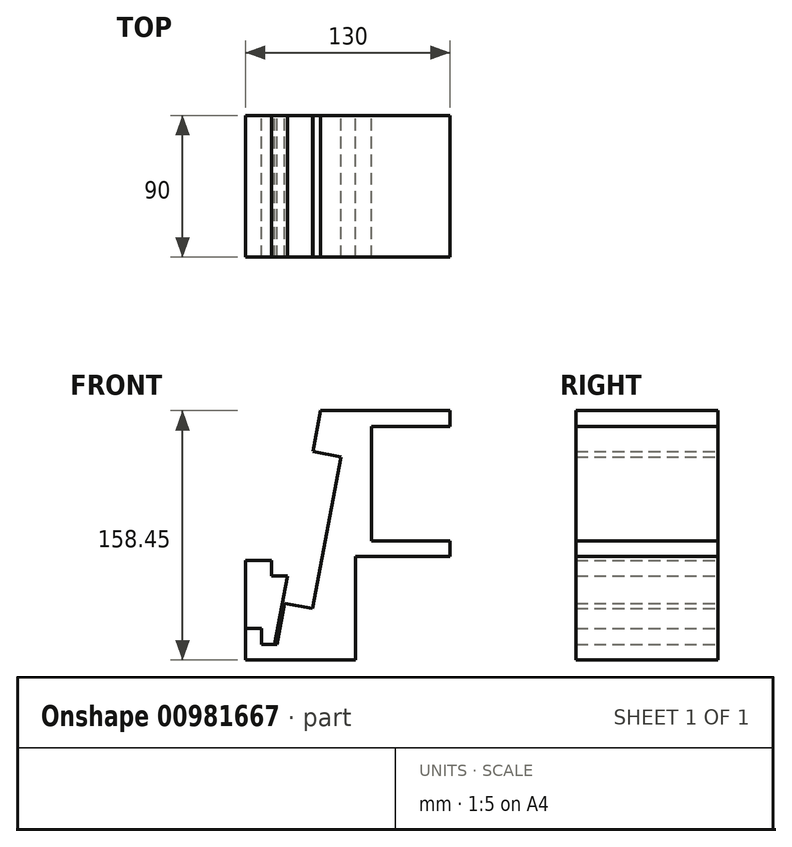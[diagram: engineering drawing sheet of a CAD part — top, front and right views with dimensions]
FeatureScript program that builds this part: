
annotation { "Feature Type Name" : "Feature", "Feature Type Description" : "" }
export const myFeature = defineFeature(function(context is Context, id is Id, definition is map)
    precondition{}
    {
        {
            var Q0;
            Q0=qCreatedBy(makeId("Front.planeOp"),FACE);
            var sketch = newSketch(context, id + "F0", { "sketchPlane" : qUnion([Q0])});
            skLineSegment(sketch, "E0", {"start": v(-40, 0) * mm, "end": v(-40, 92.76) * mm});
            skLineSegment(sketch, "E1", {"start": v(-40, 92.76) * mm, "end": v(20, 92.76) * mm});
            skLineSegment(sketch, "E2", {"start": v(20, 92.76) * mm, "end": v(20, 82.76) * mm});
            skLineSegment(sketch, "E3", {"start": v(20, 82.76) * mm, "end": v(-30, 82.76) * mm});
            skLineSegment(sketch, "E4", {"start": v(-30, 82.76) * mm, "end": v(-30, 10) * mm});
            skLineSegment(sketch, "E5", {"start": v(-30, 10) * mm, "end": v(20, 10) * mm});
            skLineSegment(sketch, "E6", {"start": v(20, 10) * mm, "end": v(20, 0) * mm});
            skLineSegment(sketch, "E7", {"start": v(20, 0) * mm, "end": v(-40, 0) * mm});
            skLineSegment(sketch, "E8", {"start": v(-40, 92.76) * mm, "end": v(-40, -65.69) * mm});
            skLineSegment(sketch, "E9", {"start": v(-40, -65.69) * mm, "end": v(-110, -65.69) * mm});
            skLineSegment(sketch, "E10", {"start": v(-110, -45.69) * mm, "end": v(-100, -45.69) * mm});
            skLineSegment(sketch, "E11", {"start": v(-100, -45.69) * mm, "end": v(-100, -55.69) * mm});
            skLineSegment(sketch, "E12", {"start": v(-100, -55.69) * mm, "end": v(-90, -55.69) * mm});
            skLineSegment(sketch, "E13", {"start": v(-90, -55.69) * mm, "end": v(-62.37, 92.76) * mm});
            skLineSegment(sketch, "E14", {"start": v(-76.19, 18.54) * mm, "end": v(-58.49, 15.24) * mm});
            skLineSegment(sketch, "E15", {"start": v(-58.49, 15.24) * mm, "end": v(-49.52, 63.42) * mm});
            skLineSegment(sketch, "E16", {"start": v(-58.49, 15.24) * mm, "end": v(-67.46, -32.93) * mm});
            skLineSegment(sketch, "E17", {"start": v(-49.52, 63.42) * mm, "end": v(-67.22, 66.71) * mm});
            skLineSegment(sketch, "E18", {"start": v(-67.46, -32.93) * mm, "end": v(-85.15, -29.64) * mm});
            skLineSegment(sketch, "E19", {"start": v(-110, -45.69) * mm, "end": v(-110, -65.69) * mm});
            skLineSegment(sketch, "E20", {"start": v(-62.37, 92.76) * mm, "end": v(-40, 92.76) * mm});
            skLineSegment(sketch, "E21", {"start": v(-110, -45.69) * mm, "end": v(-110, -2.38) * mm});
            skLineSegment(sketch, "E22", {"start": v(-91.53, -55.69) * mm, "end": v(-83.47, -12.38) * mm});
            skLineSegment(sketch, "E23", {"start": v(-83.47, -12.38) * mm, "end": v(-93.47, -12.38) * mm});
            skLineSegment(sketch, "E24", {"start": v(-93.47, -12.38) * mm, "end": v(-93.47, -2.38) * mm});
            skLineSegment(sketch, "E25", {"start": v(-93.47, -2.38) * mm, "end": v(-110, -2.38) * mm});
            skPoint(sketch, "E26.orphan", {"position": v(-100, 9.03) * mm});
            skSolve(sketch);
        }
        {
            var Q0;
            {var subQ0=sQuery(id+"F0.wireOp",EDGE,"E0");Q0=makeQuery(id+"F0.imprint","IMPRINT",FACE,{"disambiguationData":[TD([[makeQuery(id+"F0.imprint","IMPRINT",EDGE,{"derivedFrom":subQ0}),-1.0]])]});}
            var Q1;
            {var subQ6=sQuery(id+"F0.wireOp",EDGE,"I6OWvMeT-nftw-VONz-IhKe-1W3561zI6XcC");Q1=makeQuery(id+"F0.imprint","IMPRINT",FACE,{"disambiguationData":[TD([[makeQuery(id+"F0.imprint","IMPRINT",EDGE,{"derivedFrom":subQ6}),-1.0]])]});}
            var Q2;
            {var subQ7=sQuery(id+"F0.wireOp",EDGE,"E9");Q2=makeQuery(id+"F0.imprint","IMPRINT",FACE,{"disambiguationData":[TD([[makeQuery(id+"F0.imprint","IMPRINT",EDGE,{"derivedFrom":subQ7}),-1.0]])]});}
            var Q3;
            {var subQ0=sQuery(id+"F0.wireOp",EDGE,"E1");Q3=makeQuery(id+"F0.imprint","IMPRINT",FACE,{"disambiguationData":[TD([[makeQuery(id+"F0.imprint","IMPRINT",EDGE,{"derivedFrom":subQ0}),-1.0]])]});}
            extrude(context, id + "F1", {"entities" : qUnion([Q0, Q1, Q2, Q3]), "depth" : 90 * mm, "offsetDistance" : 25 * mm});
        }
        {
            var Q0;
            Q0=makeQuery(id+"F0.imprint","IMPRINT",FACE,{"disambiguationData":[TD([[makeQuery(id+"F0.imprint","IMPRINT",EDGE,{"derivedFrom":sQuery(id+"F0.wireOp",EDGE,"E10")}),1.0]])]});
            extrude(context, id + "F2", {"entities" : qUnion([Q0]), "depth" : 90 * mm, "offsetDistance" : 25 * mm});
        }
    });
